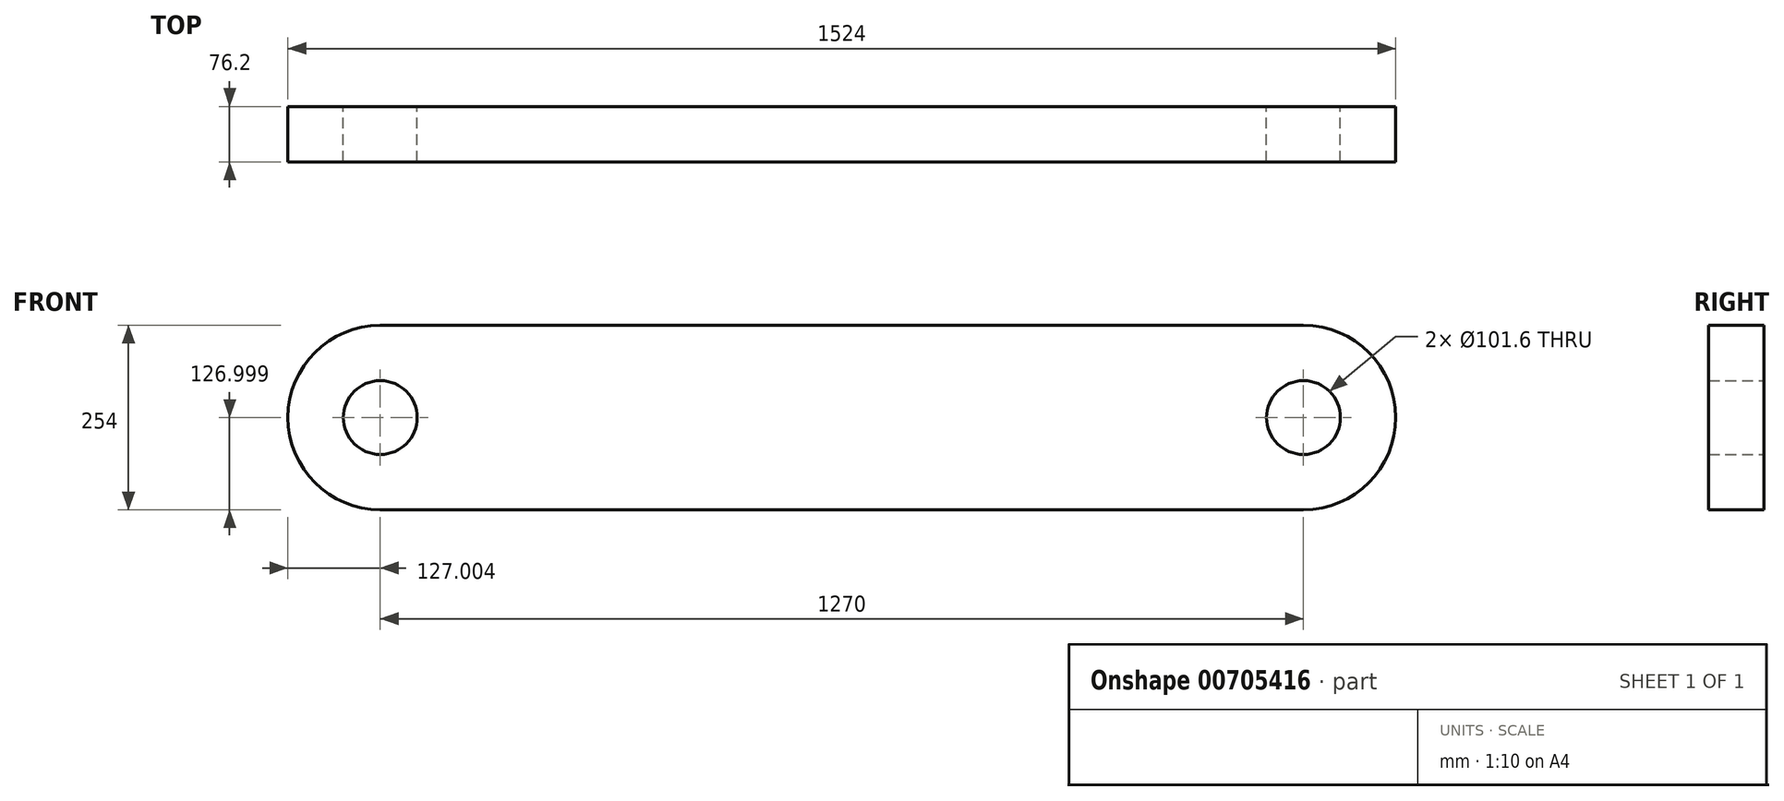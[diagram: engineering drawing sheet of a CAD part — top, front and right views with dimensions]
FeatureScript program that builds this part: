
annotation { "Feature Type Name" : "Feature", "Feature Type Description" : "" }
export const myFeature = defineFeature(function(context is Context, id is Id, definition is map)
    precondition{}
    {
        {
            var Q0;
            Q0=qCreatedBy(makeId("Front.planeOp"),FACE);
            var sketch = newSketch(context, id + "F0", { "sketchPlane" : qUnion([Q0])});
            skLineSegment(sketch, "E0", {"start": v(-624.2, 129.78) * mm, "end": v(645.8, 129.78) * mm});
            skLineSegment(sketch, "E1", {"start": v(-624.2, -124.22) * mm, "end": v(645.8, -124.22) * mm});
            skArc(sketch, "E2", {"start": v(-624.2, 129.78) * mm, "mid": v(-751.2, 2.78) * mm, "end": v(-624.2, -124.22) * mm});
            skArc(sketch, "E3", {"start": v(645.8, 129.78) * mm, "mid": v(772.8, 2.78) * mm, "end": v(645.8, -124.22) * mm});
            skCircle(sketch, "E4", {"center": v(-624.2, 2.78) * mm, "radius": 50.8 * mm});
            skCircle(sketch, "E5", {"center": v(645.8, 2.78) * mm, "radius": 50.8 * mm});
            skSolve(sketch);
        }
        {
            var Q0;
            Q0 = qSketchRegion(id + "F0", true);
            extrude(context, id + "F1", {"entities" : qUnion([Q0]), "depth" : 76.2 * mm, "offsetDistance" : 25.4 * mm});
        }
    });
